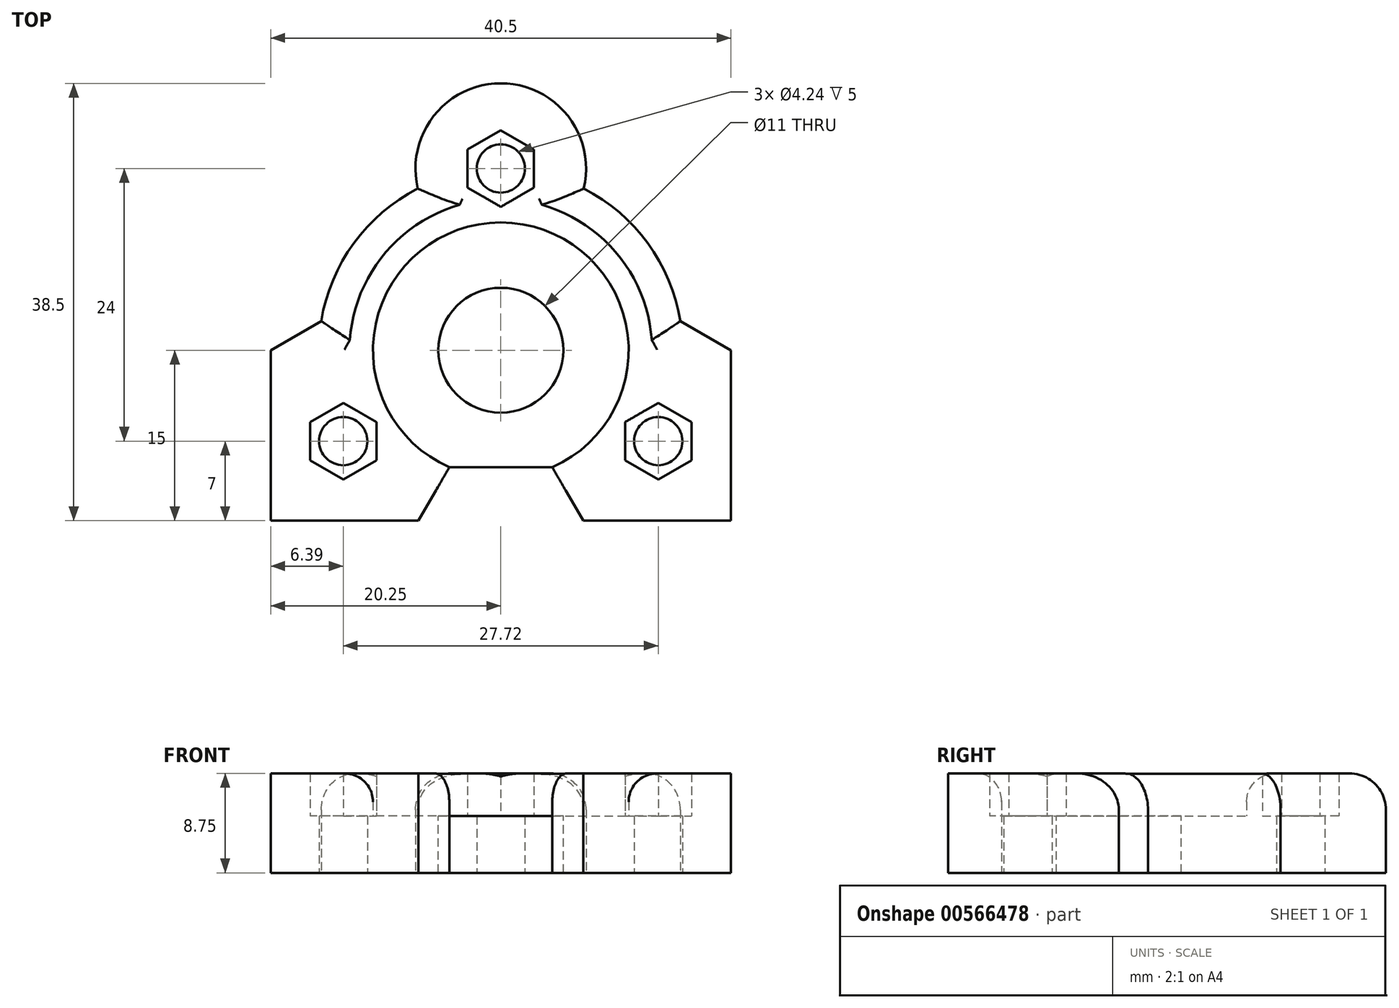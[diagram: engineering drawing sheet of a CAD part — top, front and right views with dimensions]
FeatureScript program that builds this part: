
annotation { "Feature Type Name" : "Feature", "Feature Type Description" : "" }
export const myFeature = defineFeature(function(context is Context, id is Id, definition is map)
    precondition{}
    {
        {
            var Q0;
            Q0=qCreatedBy(makeId("Top.planeOp"),FACE);
            var sketch = newSketch(context, id + "F0", { "sketchPlane" : qUnion([Q0])});
            skCircle(sketch, "E0", {"center": v(0, 0) * mm, "radius": 11.18 * mm, "construction": true});
            skLineSegment(sketch, "E1.bottom", {"start": v(25, -22.1) * mm, "end": v(-25, -22.1) * mm, "construction": true});
            skLineSegment(sketch, "E1.top", {"start": v(25, 22.1) * mm, "end": v(-25, 22.1) * mm, "construction": true});
            skLineSegment(sketch, "E1.left", {"start": v(25, -22.1) * mm, "end": v(25, 0) * mm});
            skLineSegment(sketch, "E1.right", {"start": v(-25, -22.1) * mm, "end": v(-25, 0) * mm});
            skLineSegment(sketch, "E2", {"start": v(-25, -22.1) * mm, "end": v(-25, -27.1) * mm});
            skLineSegment(sketch, "E3", {"start": v(-25, -27.1) * mm, "end": v(25, -27.1) * mm});
            skLineSegment(sketch, "E4", {"start": v(25, -27.1) * mm, "end": v(25, -22.1) * mm});
            skCircle(sketch, "E5", {"center": v(0, 0) * mm, "radius": 5.25 * mm});
            skArc(sketch, "E6", {"start": v(25, 0) * mm, "mid": v(0, 25) * mm, "end": v(-25, 0) * mm});
            skCircle(sketch, "E7", {"center": v(7.5, 0) * mm, "radius": 1.93 * mm, "construction": true});
            skCircle(sketch, "E8.1.0", {"center": v(0, 7.5) * mm, "radius": 1.93 * mm, "construction": true});
            skCircle(sketch, "E8.2.0", {"center": v(-7.5, 0) * mm, "radius": 1.93 * mm, "construction": true});
            skCircle(sketch, "E8.3.0", {"center": v(0, -7.5) * mm, "radius": 1.93 * mm, "construction": true});
            skCircle(sketch, "E9", {"center": v(0, 16) * mm, "radius": 2.12 * mm});
            skCircle(sketch, "E10.1.0", {"center": v(-13.86, -8) * mm, "radius": 2.12 * mm});
            skCircle(sketch, "E10.2.0", {"center": v(13.86, -8) * mm, "radius": 2.12 * mm});
            skSolve(sketch);
        }
        {
            var Q0;
            Q0=qSketchRegion(id+"F0",true);
            extrude(context, id + "F1", {"entities" : qUnion([Q0]), "depth" : 5 * mm});
        }
        {
            var Q0;
            Q0=makeQuery(id+"F1.opExtrude","CAP_FACE",FACE,{"disambiguationData":[OSD([sQuery(id+"F0.wireOp",EDGE,"E1.top"),sQuery(id+"F0.wireOp",EDGE,"E1.left"),sQuery(id+"F0.wireOp",EDGE,"E1.right"),sQuery(id+"F0.wireOp",EDGE,"E2"),sQuery(id+"F0.wireOp",EDGE,"E3"),sQuery(id+"F0.wireOp",EDGE,"E4"),sQuery(id+"F0.wireOp",EDGE,"E5")])],"isStart":false});
            var sketch = newSketch(context, id + "F2", { "sketchPlane" : qUnion([Q0])});
            skLineSegment(sketch, "E11.bottom", {"start": v(25, -27.1) * mm, "end": v(-25, -27.1) * mm});
            skLineSegment(sketch, "E11.top", {"start": v(21, -22.1) * mm, "end": v(5, -22.1) * mm});
            skLineSegment(sketch, "E11.left", {"start": v(25, -27.1) * mm, "end": v(25, -22.1) * mm});
            skLineSegment(sketch, "E11.right", {"start": v(-25, -27.1) * mm, "end": v(-25, -22.1) * mm});
            skPoint(sketch, "E11.middle", {"position": v(0, -24.6) * mm});
            skLineSegment(sketch, "E12", {"start": v(-5, -22.1) * mm, "end": v(-5, -14.1) * mm});
            skLineSegment(sketch, "E13", {"start": v(-5, -14.1) * mm, "end": v(0, -14.1) * mm});
            skLineSegment(sketch, "E14.MirrorCS", {"start": v(5, -14.1) * mm, "end": v(0, -14.1) * mm});
            skLineSegment(sketch, "E15.MirrorCS", {"start": v(5, -22.1) * mm, "end": v(5, -14.1) * mm});
            skLineSegment(sketch, "E16.trimOffspring", {"start": v(-5, -22.1) * mm, "end": v(-21, -22.1) * mm});
            skLineSegment(sketch, "E17", {"start": v(-25, -22.1) * mm, "end": v(-25, 0) * mm});
            skLineSegment(sketch, "E18", {"start": v(-25, 0) * mm, "end": v(-21, 0) * mm});
            skLineSegment(sketch, "E19", {"start": v(-21, 0) * mm, "end": v(-21, -22.1) * mm});
            skLineSegment(sketch, "E20.MirrorCS", {"start": v(21, 0) * mm, "end": v(21, -22.1) * mm});
            skLineSegment(sketch, "E21.MirrorCS", {"start": v(25, 0) * mm, "end": v(21, 0) * mm});
            skLineSegment(sketch, "E22.MirrorCS", {"start": v(25, -22.1) * mm, "end": v(25, 0) * mm});
            skSolve(sketch);
        }
        {
            var Q0;
            Q0=qSketchRegion(id+"F2",true);
            extrude(context, id + "F3", {"entities" : qUnion([Q0]), "operationType" : NewBodyOperationType.ADD, "depth" : 15 * mm});
        }
        {
            var Q0;
            Q0=makeQuery(id+"F3.boolean.opBoolean","MERGE",FACE,{"derivedFrom":[makeQuery(id+"F1.opExtrude","SWEPT_FACE",FACE,{"disambiguationData":[OSD([sQuery(id+"F0.wireOp",EDGE,"E3")])]}),makeQuery(id+"F3.opExtrude","SWEPT_FACE",FACE,{"disambiguationData":[OSD([sQuery(id+"F2.wireOp",EDGE,"E11.bottom")])]})]});
            var sketch = newSketch(context, id + "F4", { "sketchPlane" : qUnion([Q0])});
            skCircle(sketch, "E23", {"center": v(-11.73, 12.5) * mm, "radius": 2.12 * mm});
            skCircle(sketch, "E24.MirrorC", {"center": v(11.72, 12.5) * mm, "radius": 2.12 * mm});
            skSolve(sketch);
        }
        {
            var Q0;
            Q0=qSketchRegion(id+"F4",true);
            extrude(context, id + "F5", {"entities" : qUnion([Q0]), "operationType" : NewBodyOperationType.REMOVE, "oppositeDirection" : true, "depth" : 25 * mm});
        }
        {
            var Q0;
            Q0=qCreatedBy(makeId("Top.planeOp"),FACE);
            var sketch = newSketch(context, id + "F6", { "sketchPlane" : qUnion([Q0])});
            skLineSegment(sketch, "E25.bottom", {"start": v(25, -27.1) * mm, "end": v(-25, -27.1) * mm});
            skLineSegment(sketch, "E25.top", {"start": v(25, -42.1) * mm, "end": v(-25, -42.1) * mm});
            skLineSegment(sketch, "E25.left", {"start": v(25, -27.1) * mm, "end": v(25, -42.1) * mm});
            skLineSegment(sketch, "E25.right", {"start": v(-25, -27.1) * mm, "end": v(-25, -42.1) * mm});
            skPoint(sketch, "E25.middle", {"position": v(0, -34.6) * mm});
            skCircle(sketch, "E26", {"center": v(-17.5, -34.6) * mm, "radius": 2.12 * mm});
            skCircle(sketch, "E27.MirrorC", {"center": v(17.5, -34.6) * mm, "radius": 2.12 * mm});
            skSolve(sketch);
        }
        {
            var Q0;
            Q0=qSketchRegion(id+"F6",true);
            extrude(context, id + "F7", {"entities" : qUnion([Q0]), "operationType" : NewBodyOperationType.ADD, "depth" : 5 * mm});
        }
        {
            var Q0;
            Q0=makeQuery(id+"F7.opExtrude","SWEPT_EDGE",EDGE,{"disambiguationData":[OSD([sQuery(id+"F6.wireOp",EDGE,"E25.top"),sQuery(id+"F6.wireOp",EDGE,"E25.right")])]});
            var Q1;
            Q1=makeQuery(id+"F7.opExtrude","SWEPT_EDGE",EDGE,{"disambiguationData":[OSD([sQuery(id+"F6.wireOp",EDGE,"E25.top"),sQuery(id+"F6.wireOp",EDGE,"E25.left")])]});
            fillet(context, id + "F8", {"entities" : qUnion([Q0, Q1]), "radius" : 7.5 * mm, "tangentPropagation" : true, "allowEdgeOverflow" : false});
        }
        {
            var Q0;
            Q0=makeQuery(id+"F3.opExtrude","CAP_EDGE",EDGE,{"disambiguationData":[OSD([sQuery(id+"F2.wireOp",EDGE,"E13"),sQuery(id+"F2.wireOp",EDGE,"E14.MirrorCS")])],"isStart":false});
            var Q1;
            Q1=makeQuery(id+"F3.opExtrude","CAP_EDGE",EDGE,{"disambiguationData":[OSD([sQuery(id+"F2.wireOp",EDGE,"E18")])],"isStart":false});
            var Q2;
            Q2=makeQuery(id+"F3.opExtrude","CAP_EDGE",EDGE,{"disambiguationData":[OSD([sQuery(id+"F2.wireOp",EDGE,"E21.MirrorCS")])],"isStart":false});
            chamfer(context, id + "F9", {"entities" : qUnion([Q0, Q1, Q2]), "width" : 7.5 * mm, "tangentPropagation" : true});
        }
        {
            var Q0;
            Q0=makeQuery(id+"F1.opExtrude","CAP_FACE",FACE,{"disambiguationData":[OSD([sQuery(id+"F0.wireOp",EDGE,"E1.left"),sQuery(id+"F0.wireOp",EDGE,"E1.right"),sQuery(id+"F0.wireOp",EDGE,"E2"),sQuery(id+"F0.wireOp",EDGE,"E3"),sQuery(id+"F0.wireOp",EDGE,"E4"),sQuery(id+"F0.wireOp",EDGE,"E5"),sQuery(id+"F0.wireOp",EDGE,"E6"),sQuery(id+"F0.wireOp",EDGE,"E7"),sQuery(id+"F0.wireOp",EDGE,"E8.1.0"),sQuery(id+"F0.wireOp",EDGE,"E8.2.0"),sQuery(id+"F0.wireOp",EDGE,"E8.3.0")])],"isStart":false});
            var sketch = newSketch(context, id + "F10", { "sketchPlane" : qUnion([Q0])});
            skCircle(sketch, "E28", {"center": v(0, 0) * mm, "radius": 11.25 * mm});
            skArc(sketch, "E29", {"start": v(25, 0) * mm, "mid": v(0, 25) * mm, "end": v(-25, 0) * mm});
            skLineSegment(sketch, "E30", {"start": v(-25, 0) * mm, "end": v(-25, -22.1) * mm});
            skLineSegment(sketch, "E31", {"start": v(25, -22.1) * mm, "end": v(25, 0) * mm});
            skLineSegment(sketch, "E32", {"start": v(-25, -22.1) * mm, "end": v(25, -22.1) * mm});
            skCircle(sketch, "E33.cCircle", {"center": v(13.86, -8) * mm, "radius": 2.92 * mm, "construction": true});
            skLineSegment(sketch, "E33.0", {"start": v(16.77, -6.32) * mm, "end": v(16.77, -9.68) * mm});
            skLineSegment(sketch, "E33.1", {"start": v(16.77, -9.68) * mm, "end": v(13.86, -11.37) * mm});
            skLineSegment(sketch, "E33.2", {"start": v(13.86, -11.37) * mm, "end": v(10.94, -9.68) * mm});
            skLineSegment(sketch, "E33.3", {"start": v(10.94, -9.68) * mm, "end": v(10.94, -6.32) * mm});
            skLineSegment(sketch, "E33.4", {"start": v(10.94, -6.32) * mm, "end": v(13.86, -4.63) * mm});
            skLineSegment(sketch, "E33.5", {"start": v(13.86, -4.63) * mm, "end": v(16.77, -6.32) * mm});
            skPoint(sketch, "E33.0.midPoint", {"position": v(16.77, -8) * mm});
            skLineSegment(sketch, "E34.MirrorCS", {"start": v(-16.77, -6.32) * mm, "end": v(-16.77, -9.68) * mm});
            skLineSegment(sketch, "E35.MirrorCS", {"start": v(-13.86, -4.63) * mm, "end": v(-16.77, -6.32) * mm});
            skLineSegment(sketch, "E36.MirrorCS", {"start": v(-16.77, -9.68) * mm, "end": v(-13.86, -11.37) * mm});
            skLineSegment(sketch, "E37.MirrorCS", {"start": v(-10.94, -9.68) * mm, "end": v(-10.94, -6.32) * mm});
            skLineSegment(sketch, "E38.MirrorCS", {"start": v(-10.94, -6.32) * mm, "end": v(-13.86, -4.63) * mm});
            skLineSegment(sketch, "E39.MirrorCS", {"start": v(-13.86, -11.37) * mm, "end": v(-10.94, -9.68) * mm});
            skPoint(sketch, "E40.MirrorP", {"position": v(-16.77, -8) * mm});
            skCircle(sketch, "E41.MirrorC", {"center": v(-13.86, -8) * mm, "radius": 2.92 * mm, "construction": true});
            skCircle(sketch, "E42.cCircle", {"center": v(0, 16) * mm, "radius": 2.92 * mm, "construction": true});
            skLineSegment(sketch, "E42.0", {"start": v(2.92, 17.68) * mm, "end": v(2.92, 14.32) * mm});
            skLineSegment(sketch, "E42.1", {"start": v(2.92, 14.32) * mm, "end": v(0, 12.63) * mm});
            skLineSegment(sketch, "E42.2", {"start": v(0, 12.63) * mm, "end": v(-2.92, 14.32) * mm});
            skLineSegment(sketch, "E42.3", {"start": v(-2.92, 14.32) * mm, "end": v(-2.92, 17.68) * mm});
            skLineSegment(sketch, "E42.4", {"start": v(-2.92, 17.68) * mm, "end": v(0, 19.37) * mm});
            skLineSegment(sketch, "E42.5", {"start": v(0, 19.37) * mm, "end": v(2.92, 17.68) * mm});
            skPoint(sketch, "E42.0.midPoint", {"position": v(2.92, 16) * mm});
            skSolve(sketch);
        }
        {
            var Q0;
            Q0=qSketchRegion(id+"F10",true);
            extrude(context, id + "F11", {"entities" : qUnion([Q0]), "operationType" : NewBodyOperationType.ADD, "depth" : 3.75 * mm});
        }
        {
            var Q0;
            Q0=makeQuery(id+"F11.boolean.opBoolean","INTERSECT",EDGE,{"derivedFrom":[makeQuery(id+"F3.opExtrude","SWEPT_FACE",FACE,{"disambiguationData":[OSD([sQuery(id+"F2.wireOp",EDGE,"E13"),sQuery(id+"F2.wireOp",EDGE,"E14.MirrorCS")])]}),makeQuery(id+"F11.opExtrude","CAP_FACE",FACE,{"disambiguationData":[OSD([sQuery(id+"F10.wireOp",EDGE,"E28"),sQuery(id+"F10.wireOp",EDGE,"E29"),sQuery(id+"F10.wireOp",EDGE,"E30"),sQuery(id+"F10.wireOp",EDGE,"KMwbHocN-jLKF-1fT8-stF3-EZ2oOHbS1cSO"),sQuery(id+"F10.wireOp",EDGE,"Onsy7AXm-IlgJ-wlJu-APFR-eMNSHrUauErb"),sQuery(id+"F10.wireOp",EDGE,"E31")])],"isStart":false})]});
            var Q1;
            Q1=makeQuery(id+"F11.boolean.opBoolean","INTERSECT",EDGE,{"derivedFrom":[makeQuery(id+"F3.opExtrude","SWEPT_FACE",FACE,{"disambiguationData":[OSD([sQuery(id+"F2.wireOp",EDGE,"E18")])]}),makeQuery(id+"F11.opExtrude","CAP_FACE",FACE,{"disambiguationData":[OSD([sQuery(id+"F10.wireOp",EDGE,"E28"),sQuery(id+"F10.wireOp",EDGE,"E29"),sQuery(id+"F10.wireOp",EDGE,"E30"),sQuery(id+"F10.wireOp",EDGE,"KMwbHocN-jLKF-1fT8-stF3-EZ2oOHbS1cSO"),sQuery(id+"F10.wireOp",EDGE,"Onsy7AXm-IlgJ-wlJu-APFR-eMNSHrUauErb"),sQuery(id+"F10.wireOp",EDGE,"E31")])],"isStart":false})]});
            var Q2;
            Q2=makeQuery(id+"F11.boolean.opBoolean","INTERSECT",EDGE,{"derivedFrom":[makeQuery(id+"F3.opExtrude","SWEPT_FACE",FACE,{"disambiguationData":[OSD([sQuery(id+"F2.wireOp",EDGE,"E21.MirrorCS")])]}),makeQuery(id+"F11.opExtrude","CAP_FACE",FACE,{"disambiguationData":[OSD([sQuery(id+"F10.wireOp",EDGE,"E29"),sQuery(id+"F10.wireOp",EDGE,"E30"),sQuery(id+"F10.wireOp",EDGE,"E31"),sQuery(id+"F10.wireOp",EDGE,"E32"),sQuery(id+"F10.wireOp",EDGE,"E33.0"),sQuery(id+"F10.wireOp",EDGE,"E33.1"),sQuery(id+"F10.wireOp",EDGE,"E33.2"),sQuery(id+"F10.wireOp",EDGE,"E33.3"),sQuery(id+"F10.wireOp",EDGE,"E33.4"),sQuery(id+"F10.wireOp",EDGE,"E33.5"),sQuery(id+"F10.wireOp",EDGE,"E34.MirrorCS"),sQuery(id+"F10.wireOp",EDGE,"E35.MirrorCS"),sQuery(id+"F10.wireOp",EDGE,"E36.MirrorCS"),sQuery(id+"F10.wireOp",EDGE,"E37.MirrorCS"),sQuery(id+"F10.wireOp",EDGE,"E38.MirrorCS"),sQuery(id+"F10.wireOp",EDGE,"E28"),sQuery(id+"F10.wireOp",EDGE,"E39.MirrorCS"),sQuery(id+"F10.wireOp",EDGE,"E42.0"),sQuery(id+"F10.wireOp",EDGE,"E42.1"),sQuery(id+"F10.wireOp",EDGE,"E42.2"),sQuery(id+"F10.wireOp",EDGE,"E42.3"),sQuery(id+"F10.wireOp",EDGE,"E42.4"),sQuery(id+"F10.wireOp",EDGE,"E42.5")])],"isStart":false})]});
            chamfer(context, id + "F12", {"entities" : qUnion([Q0, Q1, Q2]), "width" : 2.5 * mm, "tangentPropagation" : true});
        }
        {
            var Q0;
            Q0=makeQuery(id+"F9.opChamfer","BLEND_EDGE",EDGE,{"blendedFrom":[makeQuery(id+"F3.opExtrude","CAP_EDGE",EDGE,{"disambiguationData":[OSD([sQuery(id+"F2.wireOp",EDGE,"E13"),sQuery(id+"F2.wireOp",EDGE,"E14.MirrorCS")])],"isStart":false}),makeQuery(id+"F3.opExtrude","SWEPT_FACE",FACE,{"disambiguationData":[OSD([sQuery(id+"F2.wireOp",EDGE,"E15.MirrorCS")])]})],"blendedInto":[makeQuery(id+"F3.opExtrude","SWEPT_FACE",FACE,{"disambiguationData":[OSD([sQuery(id+"F2.wireOp",EDGE,"E15.MirrorCS")])]})]});
            var Q1;
            Q1=makeQuery(id+"F9.opChamfer","BLEND_EDGE",EDGE,{"blendedFrom":[makeQuery(id+"F3.opExtrude","CAP_EDGE",EDGE,{"disambiguationData":[OSD([sQuery(id+"F2.wireOp",EDGE,"E13"),sQuery(id+"F2.wireOp",EDGE,"E14.MirrorCS")])],"isStart":false}),makeQuery(id+"F3.opExtrude","SWEPT_FACE",FACE,{"disambiguationData":[OSD([sQuery(id+"F2.wireOp",EDGE,"E12")])]})],"blendedInto":[makeQuery(id+"F3.opExtrude","SWEPT_FACE",FACE,{"disambiguationData":[OSD([sQuery(id+"F2.wireOp",EDGE,"E12")])]})]});
            fillet(context, id + "F13", {"entities" : qUnion([Q0, Q1]), "radius" : 5 * mm, "tangentPropagation" : true, "allowEdgeOverflow" : false});
        }
        {
            var Q0;
            Q0=makeQuery(id+"F3.opExtrude","CAP_EDGE",EDGE,{"disambiguationData":[OSD([sQuery(id+"F2.wireOp",EDGE,"E20.MirrorCS")])],"isStart":false});
            var Q1;
            Q1=makeQuery(id+"F3.opExtrude","CAP_EDGE",EDGE,{"disambiguationData":[OSD([sQuery(id+"F2.wireOp",EDGE,"E11.left"),sQuery(id+"F2.wireOp",EDGE,"E22.MirrorCS")])],"isStart":false});
            var Q2;
            Q2=makeQuery(id+"F3.opExtrude","CAP_EDGE",EDGE,{"disambiguationData":[OSD([sQuery(id+"F2.wireOp",EDGE,"E19")])],"isStart":false});
            var Q3;
            Q3=makeQuery(id+"F3.opExtrude","CAP_EDGE",EDGE,{"disambiguationData":[OSD([sQuery(id+"F2.wireOp",EDGE,"E11.right"),sQuery(id+"F2.wireOp",EDGE,"E17")])],"isStart":false});
            fillet(context, id + "F14", {"entities" : qUnion([Q0, Q1, Q2, Q3]), "radius" : 2 * mm, "tangentPropagation" : true, "allowEdgeOverflow" : false});
        }
        {
            var Q0;
            Q0=makeQuery(id+"F1.opExtrude","CAP_FACE",FACE,{"disambiguationData":[OSD([sQuery(id+"F0.wireOp",EDGE,"E1.left"),sQuery(id+"F0.wireOp",EDGE,"E1.right"),sQuery(id+"F0.wireOp",EDGE,"E2"),sQuery(id+"F0.wireOp",EDGE,"E3"),sQuery(id+"F0.wireOp",EDGE,"E4"),sQuery(id+"F0.wireOp",EDGE,"E5"),sQuery(id+"F0.wireOp",EDGE,"E6"),sQuery(id+"F0.wireOp",EDGE,"E7"),sQuery(id+"F0.wireOp",EDGE,"E8.1.0"),sQuery(id+"F0.wireOp",EDGE,"E8.2.0"),sQuery(id+"F0.wireOp",EDGE,"E8.3.0")])],"isStart":false});
            var sketch = newSketch(context, id + "F15", { "sketchPlane" : qUnion([Q0])});
            skCircle(sketch, "E43", {"center": v(0, 0) * mm, "radius": 5.5 * mm});
            skSolve(sketch);
        }
        {
            var Q0;
            Q0=qSketchRegion(id+"F15",true);
            extrude(context, id + "F16", {"entities" : qUnion([Q0]), "operationType" : NewBodyOperationType.REMOVE, "oppositeDirection" : true, "depth" : 25 * mm});
        }
        {
            var Q0;
            {var subQ0=sQuery(id+"F0.wireOp",EDGE,"E5");Q0=makeQuery(id+"F11.boolean.opBoolean","SPLIT",FACE,{"disambiguationData":[TD([makeQuery(id+"F1.opExtrude","SWEPT_FACE",FACE,{"disambiguationData":[OSD([subQ0])]})])],"derivedFrom":makeQuery(id+"F1.opExtrude","CAP_FACE",FACE,{"disambiguationData":[OSD([sQuery(id+"F0.wireOp",EDGE,"E1.left"),sQuery(id+"F0.wireOp",EDGE,"E1.right"),sQuery(id+"F0.wireOp",EDGE,"E2"),sQuery(id+"F0.wireOp",EDGE,"E3"),sQuery(id+"F0.wireOp",EDGE,"E4"),subQ0,sQuery(id+"F0.wireOp",EDGE,"E6"),sQuery(id+"F0.wireOp",EDGE,"E9"),sQuery(id+"F0.wireOp",EDGE,"E10.1.0"),sQuery(id+"F0.wireOp",EDGE,"E10.2.0")])],"isStart":false})});}
            var sketch = newSketch(context, id + "F17", { "sketchPlane" : qUnion([Q0])});
            skArc(sketch, "E44", {"start": v(7.3, 14.24) * mm, "mid": v(12.93, 9.42) * mm, "end": v(15.8, 2.57) * mm});
            skArc(sketch, "E45.MirrorCS", {"start": v(-7.3, 14.24) * mm, "mid": v(-12.93, 9.42) * mm, "end": v(-15.8, 2.57) * mm});
            skArc(sketch, "E46", {"start": v(-7.3, 14.24) * mm, "mid": v(0, 23.5) * mm, "end": v(7.3, 14.24) * mm});
            skLineSegment(sketch, "E47", {"start": v(-20.25, 0) * mm, "end": v(-20.25, -15) * mm});
            skLineSegment(sketch, "E48", {"start": v(-20.25, -15) * mm, "end": v(-7.25, -15) * mm});
            skLineSegment(sketch, "E49", {"start": v(-7.25, -15) * mm, "end": v(-4.53, -10.3) * mm});
            skLineSegment(sketch, "E50", {"start": v(-4.53, -10.3) * mm, "end": v(4.53, -10.3) * mm});
            skLineSegment(sketch, "E51", {"start": v(4.53, -10.3) * mm, "end": v(7.25, -15) * mm});
            skLineSegment(sketch, "E52", {"start": v(7.25, -15) * mm, "end": v(20.25, -15) * mm});
            skLineSegment(sketch, "E53", {"start": v(20.25, -15) * mm, "end": v(20.25, 0) * mm});
            skLineSegment(sketch, "E54", {"start": v(20.25, 0) * mm, "end": v(15.8, 2.57) * mm});
            skLineSegment(sketch, "E55", {"start": v(-20.25, 0) * mm, "end": v(-15.8, 2.57) * mm});
            skLineSegment(sketch, "E56", {"start": v(-25, 0) * mm, "end": v(-25, -42.1) * mm});
            skLineSegment(sketch, "E57", {"start": v(-25, -42.1) * mm, "end": v(0, -42.1) * mm});
            skArc(sketch, "E58", {"start": v(-25, 0) * mm, "mid": v(-17.68, 17.68) * mm, "end": v(0, 25) * mm});
            skArc(sketch, "E59.MirrorCS", {"start": v(25, 0) * mm, "mid": v(17.68, 17.68) * mm, "end": v(0, 25) * mm});
            skLineSegment(sketch, "E60.MirrorCS", {"start": v(25, 0) * mm, "end": v(25, -42.1) * mm});
            skLineSegment(sketch, "E61.MirrorCS", {"start": v(25, -42.1) * mm, "end": v(0, -42.1) * mm});
            skSolve(sketch);
        }
        {
            var Q0;
            Q0=qSketchRegion(id+"F17",true);
            extrude(context, id + "F18", {"entities" : qUnion([Q0]), "operationType" : NewBodyOperationType.REMOVE, "endBound" : BoundingType.SYMMETRIC, "depth" : 35 * mm});
        }
        {
            var Q0;
            Q0=makeQuery(id+"F18.boolean.opBoolean","INTERSECT",EDGE,{"derivedFrom":[makeQuery(id+"F11.opExtrude","CAP_FACE",FACE,{"disambiguationData":[OSD([sQuery(id+"F10.wireOp",EDGE,"E29"),sQuery(id+"F10.wireOp",EDGE,"E30"),sQuery(id+"F10.wireOp",EDGE,"E31"),sQuery(id+"F10.wireOp",EDGE,"E32"),sQuery(id+"F10.wireOp",EDGE,"E33.0"),sQuery(id+"F10.wireOp",EDGE,"E33.1"),sQuery(id+"F10.wireOp",EDGE,"E33.2"),sQuery(id+"F10.wireOp",EDGE,"E33.3"),sQuery(id+"F10.wireOp",EDGE,"E33.4"),sQuery(id+"F10.wireOp",EDGE,"E33.5"),sQuery(id+"F10.wireOp",EDGE,"E34.MirrorCS"),sQuery(id+"F10.wireOp",EDGE,"E35.MirrorCS"),sQuery(id+"F10.wireOp",EDGE,"E36.MirrorCS"),sQuery(id+"F10.wireOp",EDGE,"E37.MirrorCS"),sQuery(id+"F10.wireOp",EDGE,"E38.MirrorCS"),sQuery(id+"F10.wireOp",EDGE,"E28"),sQuery(id+"F10.wireOp",EDGE,"E39.MirrorCS"),sQuery(id+"F10.wireOp",EDGE,"E42.0"),sQuery(id+"F10.wireOp",EDGE,"E42.1"),sQuery(id+"F10.wireOp",EDGE,"E42.2"),sQuery(id+"F10.wireOp",EDGE,"E42.3"),sQuery(id+"F10.wireOp",EDGE,"E42.4"),sQuery(id+"F10.wireOp",EDGE,"E42.5")])],"isStart":false}),makeQuery(id+"F18.opExtrude","SWEPT_FACE",FACE,{"disambiguationData":[OSD([sQuery(id+"F17.wireOp",EDGE,"E46")])]})]});
            var Q1;
            Q1=makeQuery(id+"F18.boolean.opBoolean","INTERSECT",EDGE,{"derivedFrom":[makeQuery(id+"F11.opExtrude","CAP_FACE",FACE,{"disambiguationData":[OSD([sQuery(id+"F10.wireOp",EDGE,"E29"),sQuery(id+"F10.wireOp",EDGE,"E30"),sQuery(id+"F10.wireOp",EDGE,"E31"),sQuery(id+"F10.wireOp",EDGE,"E32"),sQuery(id+"F10.wireOp",EDGE,"E33.0"),sQuery(id+"F10.wireOp",EDGE,"E33.1"),sQuery(id+"F10.wireOp",EDGE,"E33.2"),sQuery(id+"F10.wireOp",EDGE,"E33.3"),sQuery(id+"F10.wireOp",EDGE,"E33.4"),sQuery(id+"F10.wireOp",EDGE,"E33.5"),sQuery(id+"F10.wireOp",EDGE,"E34.MirrorCS"),sQuery(id+"F10.wireOp",EDGE,"E35.MirrorCS"),sQuery(id+"F10.wireOp",EDGE,"E36.MirrorCS"),sQuery(id+"F10.wireOp",EDGE,"E37.MirrorCS"),sQuery(id+"F10.wireOp",EDGE,"E38.MirrorCS"),sQuery(id+"F10.wireOp",EDGE,"E28"),sQuery(id+"F10.wireOp",EDGE,"E39.MirrorCS"),sQuery(id+"F10.wireOp",EDGE,"E42.0"),sQuery(id+"F10.wireOp",EDGE,"E42.1"),sQuery(id+"F10.wireOp",EDGE,"E42.2"),sQuery(id+"F10.wireOp",EDGE,"E42.3"),sQuery(id+"F10.wireOp",EDGE,"E42.4"),sQuery(id+"F10.wireOp",EDGE,"E42.5")])],"isStart":false}),makeQuery(id+"F18.opExtrude","SWEPT_FACE",FACE,{"disambiguationData":[OSD([sQuery(id+"F17.wireOp",EDGE,"E45.MirrorCS")])]})]});
            var Q2;
            Q2=makeQuery(id+"F18.boolean.opBoolean","INTERSECT",EDGE,{"derivedFrom":[makeQuery(id+"F11.opExtrude","CAP_FACE",FACE,{"disambiguationData":[OSD([sQuery(id+"F10.wireOp",EDGE,"E29"),sQuery(id+"F10.wireOp",EDGE,"E30"),sQuery(id+"F10.wireOp",EDGE,"E31"),sQuery(id+"F10.wireOp",EDGE,"E32"),sQuery(id+"F10.wireOp",EDGE,"E33.0"),sQuery(id+"F10.wireOp",EDGE,"E33.1"),sQuery(id+"F10.wireOp",EDGE,"E33.2"),sQuery(id+"F10.wireOp",EDGE,"E33.3"),sQuery(id+"F10.wireOp",EDGE,"E33.4"),sQuery(id+"F10.wireOp",EDGE,"E33.5"),sQuery(id+"F10.wireOp",EDGE,"E34.MirrorCS"),sQuery(id+"F10.wireOp",EDGE,"E35.MirrorCS"),sQuery(id+"F10.wireOp",EDGE,"E36.MirrorCS"),sQuery(id+"F10.wireOp",EDGE,"E37.MirrorCS"),sQuery(id+"F10.wireOp",EDGE,"E38.MirrorCS"),sQuery(id+"F10.wireOp",EDGE,"E28"),sQuery(id+"F10.wireOp",EDGE,"E39.MirrorCS"),sQuery(id+"F10.wireOp",EDGE,"E42.0"),sQuery(id+"F10.wireOp",EDGE,"E42.1"),sQuery(id+"F10.wireOp",EDGE,"E42.2"),sQuery(id+"F10.wireOp",EDGE,"E42.3"),sQuery(id+"F10.wireOp",EDGE,"E42.4"),sQuery(id+"F10.wireOp",EDGE,"E42.5")])],"isStart":false}),makeQuery(id+"F18.opExtrude","SWEPT_FACE",FACE,{"disambiguationData":[OSD([sQuery(id+"F17.wireOp",EDGE,"E44")])]})]});
            var Q3;
            Q3=makeQuery(id+"F18.boolean.opBoolean","INTERSECT",EDGE,{"derivedFrom":[makeQuery(id+"F11.opExtrude","CAP_FACE",FACE,{"disambiguationData":[OSD([sQuery(id+"F10.wireOp",EDGE,"E29"),sQuery(id+"F10.wireOp",EDGE,"E30"),sQuery(id+"F10.wireOp",EDGE,"E31"),sQuery(id+"F10.wireOp",EDGE,"E32"),sQuery(id+"F10.wireOp",EDGE,"E33.0"),sQuery(id+"F10.wireOp",EDGE,"E33.1"),sQuery(id+"F10.wireOp",EDGE,"E33.2"),sQuery(id+"F10.wireOp",EDGE,"E33.3"),sQuery(id+"F10.wireOp",EDGE,"E33.4"),sQuery(id+"F10.wireOp",EDGE,"E33.5"),sQuery(id+"F10.wireOp",EDGE,"E34.MirrorCS"),sQuery(id+"F10.wireOp",EDGE,"E35.MirrorCS"),sQuery(id+"F10.wireOp",EDGE,"E36.MirrorCS"),sQuery(id+"F10.wireOp",EDGE,"E37.MirrorCS"),sQuery(id+"F10.wireOp",EDGE,"E38.MirrorCS"),sQuery(id+"F10.wireOp",EDGE,"E28"),sQuery(id+"F10.wireOp",EDGE,"E39.MirrorCS"),sQuery(id+"F10.wireOp",EDGE,"E42.0"),sQuery(id+"F10.wireOp",EDGE,"E42.1"),sQuery(id+"F10.wireOp",EDGE,"E42.2"),sQuery(id+"F10.wireOp",EDGE,"E42.3"),sQuery(id+"F10.wireOp",EDGE,"E42.4"),sQuery(id+"F10.wireOp",EDGE,"E42.5")])],"isStart":false}),makeQuery(id+"F18.opExtrude","SWEPT_FACE",FACE,{"disambiguationData":[OSD([sQuery(id+"F17.wireOp",EDGE,"E55")])]})]});
            var Q4;
            Q4=makeQuery(id+"F18.boolean.opBoolean","INTERSECT",EDGE,{"derivedFrom":[makeQuery(id+"F11.opExtrude","CAP_FACE",FACE,{"disambiguationData":[OSD([sQuery(id+"F10.wireOp",EDGE,"E29"),sQuery(id+"F10.wireOp",EDGE,"E30"),sQuery(id+"F10.wireOp",EDGE,"E31"),sQuery(id+"F10.wireOp",EDGE,"E32"),sQuery(id+"F10.wireOp",EDGE,"E33.0"),sQuery(id+"F10.wireOp",EDGE,"E33.1"),sQuery(id+"F10.wireOp",EDGE,"E33.2"),sQuery(id+"F10.wireOp",EDGE,"E33.3"),sQuery(id+"F10.wireOp",EDGE,"E33.4"),sQuery(id+"F10.wireOp",EDGE,"E33.5"),sQuery(id+"F10.wireOp",EDGE,"E34.MirrorCS"),sQuery(id+"F10.wireOp",EDGE,"E35.MirrorCS"),sQuery(id+"F10.wireOp",EDGE,"E36.MirrorCS"),sQuery(id+"F10.wireOp",EDGE,"E37.MirrorCS"),sQuery(id+"F10.wireOp",EDGE,"E38.MirrorCS"),sQuery(id+"F10.wireOp",EDGE,"E28"),sQuery(id+"F10.wireOp",EDGE,"E39.MirrorCS"),sQuery(id+"F10.wireOp",EDGE,"E42.0"),sQuery(id+"F10.wireOp",EDGE,"E42.1"),sQuery(id+"F10.wireOp",EDGE,"E42.2"),sQuery(id+"F10.wireOp",EDGE,"E42.3"),sQuery(id+"F10.wireOp",EDGE,"E42.4"),sQuery(id+"F10.wireOp",EDGE,"E42.5")])],"isStart":false}),makeQuery(id+"F18.opExtrude","SWEPT_FACE",FACE,{"disambiguationData":[OSD([sQuery(id+"F17.wireOp",EDGE,"E54")])]})]});
            fillet(context, id + "F19", {"entities" : qUnion([Q0, Q1, Q2, Q3, Q4]), "radius" : 3.2 * mm, "tangentPropagation" : true, "allowEdgeOverflow" : false});
        }
        {
            var Q0;
            Q0=makeQuery(id+"F11.opExtrude","CAP_EDGE",EDGE,{"disambiguationData":[OSD([sQuery(id+"F10.wireOp",EDGE,"E28")])],"isStart":false});
            fillet(context, id + "F20", {"entities" : qUnion([Q0]), "radius" : 2.5 * mm, "tangentPropagation" : true, "allowEdgeOverflow" : false});
        }
    });
